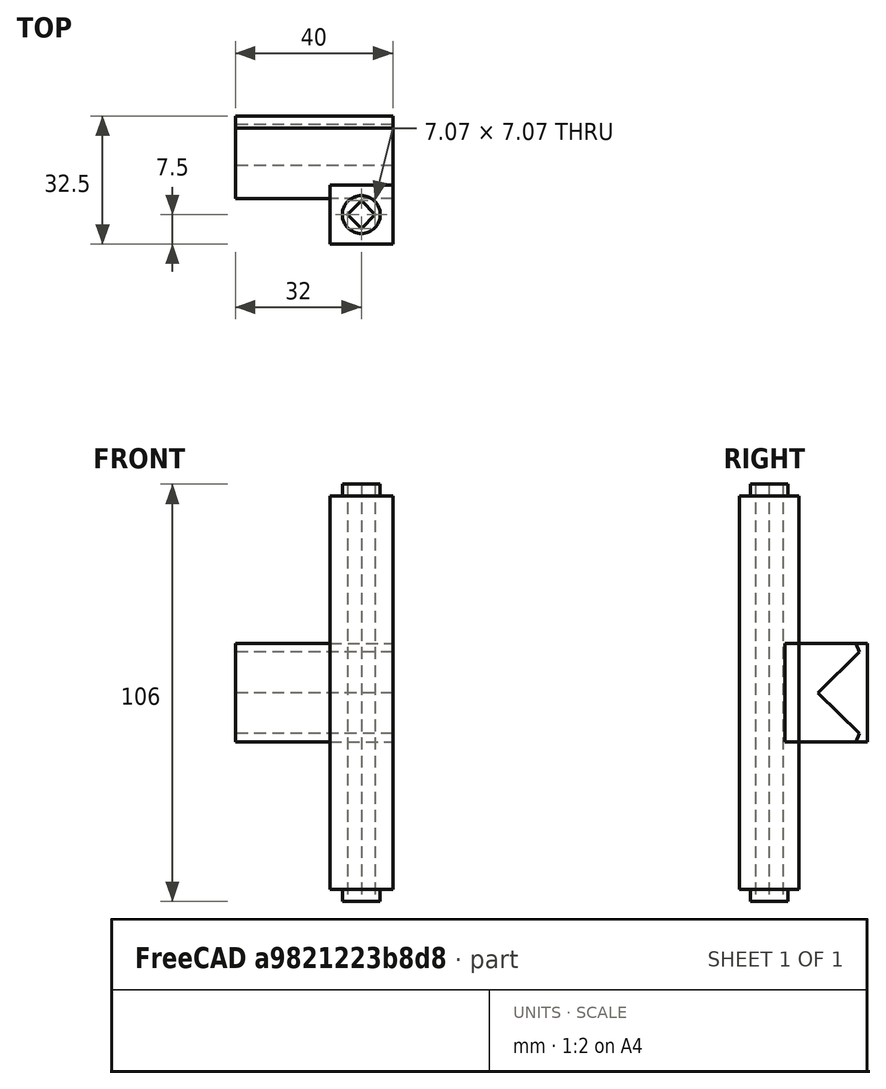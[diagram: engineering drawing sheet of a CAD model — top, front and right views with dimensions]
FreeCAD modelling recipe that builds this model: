
FCSTD DOCUMENT  (FreeCAD 0.16R)
Label: 100mmFalseAxleWithBlock
License: All rights reserved
LicenseURL: http://en.wikipedia.org/wiki/All_rights_reserved
objects: Sketcher::SketchObject×5, PartDesign::Pad×3, PartDesign::Pocket×2, PartDesign::Chamfer×1, Part::MultiFuse×1, Mesh::Feature×1
note: 17 computed .brp shape members not serialized (recipe doc carries the construction recipe); baked Part::Feature solids carry a one-line shape summary decoded from their .brp

FEATURE [Sketcher::SketchObject] Sketch
  sketch-geometry (4):
    g0: LineSegment StartX=-8 StartY=7.5 StartZ=0 EndX=8 EndY=7.5 EndZ=0
    g1: LineSegment StartX=8 StartY=7.5 StartZ=0 EndX=8 EndY=-7.5 EndZ=0
    g2: LineSegment StartX=8 StartY=-7.5 StartZ=0 EndX=-8 EndY=-7.5 EndZ=0
    g3: LineSegment StartX=-8 StartY=-7.5 StartZ=0 EndX=-8 EndY=7.5 EndZ=0
  constraints (11):
    c: Coincident(g0,g1)
    c: Coincident(g1,g2)
    c: Coincident(g2,g3)
    c: Coincident(g3,g0)
    c: Horizontal(g0)
    c: Horizontal(g2)
    c: Vertical(g1)
    c: Vertical(g3)
    c: Distance(g0) = 16
    c: Distance(g1) = 15
    c: Symmetric(g0,g2,g-1)
FEATURE [PartDesign::Pad] Pad
  Length = 100
  Length2 = 100
  Midplane = true
  Sketch = -> Sketch
  Type = 0
FEATURE [Sketcher::SketchObject] Sketch001
  Placement = pos=(0,0,50) rot=(0,0,1;0rad)
  Support = -> Pad [Face6]
  sketch-geometry (1):
    g0: Circle CenterX=0 CenterY=0 CenterZ=0 NormalX=0 NormalY=0 NormalZ=1 Radius=4.8
  constraints (2):
    c: Radius(g0) = 4.8
    c: Coincident(g0,g-1)
FEATURE [Sketcher::SketchObject] Sketch003
  sketch-geometry (4):
    g0: LineSegment StartX=-32 StartY=25 StartZ=0 EndX=8 EndY=25 EndZ=0
    g1: LineSegment StartX=8 StartY=25 StartZ=0 EndX=8 EndY=4 EndZ=0
    g2: LineSegment StartX=8 StartY=4 StartZ=0 EndX=-32 EndY=4 EndZ=0
    g3: LineSegment StartX=-32 StartY=4 StartZ=0 EndX=-32 EndY=25 EndZ=0
  constraints (12):
    c: Coincident(g0,g1)
    c: Coincident(g1,g2)
    c: Coincident(g2,g3)
    c: Coincident(g3,g0)
    c: Horizontal(g0)
    c: Horizontal(g2)
    c: Vertical(g1)
    c: Vertical(g3)
    c: Distance(g2) = 40
    c: DistanceX(g1) = 8
    c: Distance(g1) = 21
    c: DistanceY(g1) = 4
FEATURE [PartDesign::Pad] Pad002
  Length = 25
  Length2 = 100
  Midplane = true
  Sketch = -> Sketch003
  Type = 0
FEATURE [Sketcher::SketchObject] Sketch004
  ExternalGeometry = -> [Pad002]
  Placement = pos=(8,0,0) rot=(0.57735,0.57735,0.57735;2.0944rad)
  Support = -> Pad002 [Face2]
  sketch-geometry (3):
    g0: LineSegment StartX=25 StartY=12.5 StartZ=0 EndX=12.3792 EndY=0 EndZ=0
    g1: LineSegment StartX=12.3792 StartY=0 StartZ=0 EndX=25 EndY=-12.5 EndZ=0
    g2: LineSegment StartX=25 StartY=-12.5 StartZ=0 EndX=25 EndY=12.5 EndZ=0
  constraints (8):
    c: Coincident(g0,g1)
    c: Coincident(g1,g2)
    c: Coincident(g2,g0)
    c: Vertical(g2)
    c: Coincident(g0,g-3)
    c: Coincident(g1,g-4)
    c: Equal(g1,g0)
    c: Distance(g1) = 17.7633
FEATURE [PartDesign::Pocket] Pocket001
  Length = 5
  Sketch = -> Sketch004
  Type = 1
FEATURE [PartDesign::Chamfer] Chamfer
  Base = -> Pocket001 [Edge1,Edge15]
  Size = 3
FEATURE [PartDesign::Pad] Pad003
  Length = 3
  Length2 = 103
  Sketch = -> Sketch001
  Type = 4
FEATURE [Sketcher::SketchObject] Sketch002
  Placement = pos=(0,0,53) rot=(0,0,1;0rad)
  Support = -> Pad003 [Face10]
  sketch-geometry (4):
    g0: LineSegment StartX=-3.53553 StartY=0 StartZ=0 EndX=0 EndY=3.53553 EndZ=0
    g1: LineSegment StartX=0 StartY=3.53553 StartZ=0 EndX=3.53553 EndY=0 EndZ=0
    g2: LineSegment StartX=3.53553 StartY=0 StartZ=0 EndX=0 EndY=-3.53553 EndZ=0
    g3: LineSegment StartX=0 StartY=-3.53553 StartZ=0 EndX=-3.53553 EndY=0 EndZ=0
  constraints (11):
    c: Coincident(g0,g1)
    c: Coincident(g1,g2)
    c: Coincident(g2,g3)
    c: Coincident(g3,g0)
    c: Distance(g1) = 5
    c: Distance(g0) = 5
    c: Angle(g0) = 0.785398
    c: Angle(g3,g0) = 1.5708
    c: Angle(g2,g3) = 1.5708
    c: Distance(g2) = 5
    c: Symmetric(g1,g0,g-1)
FEATURE [PartDesign::Pocket] Pocket
  Length = 5
  Sketch = -> Sketch002
  Type = 1
FEATURE [Part::MultiFuse] Fusion
  Shapes = -> [Chamfer,Pocket]
FEATURE [Mesh::Feature] Mesh  label="Fusion (Meshed)"
